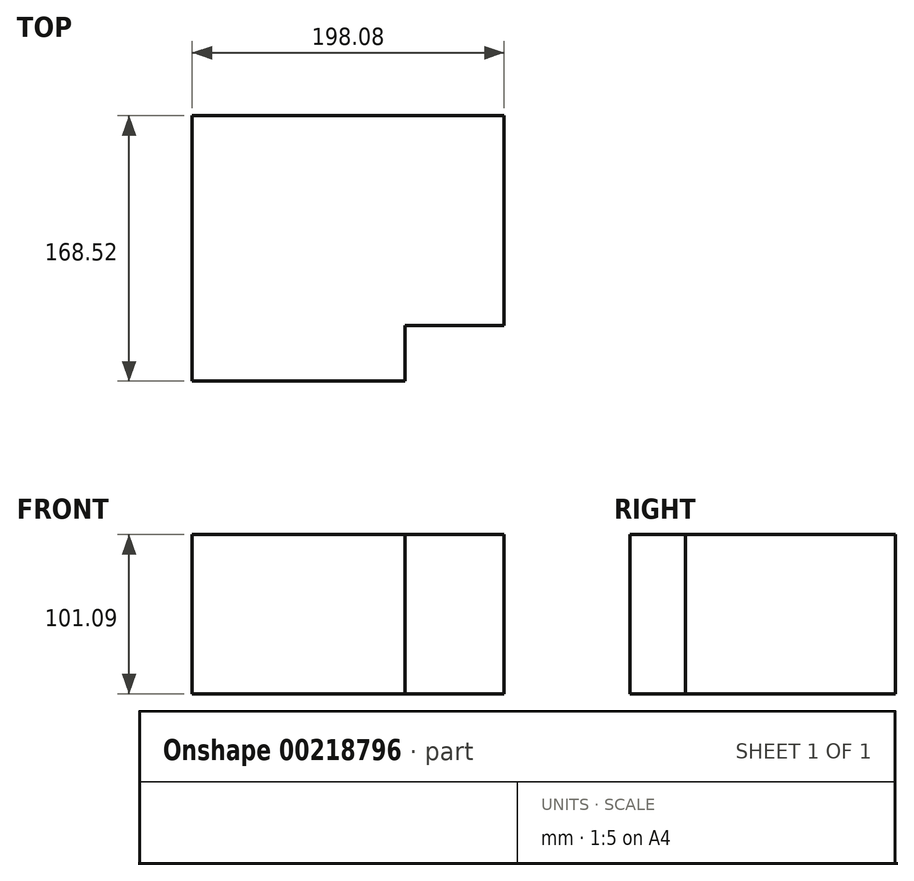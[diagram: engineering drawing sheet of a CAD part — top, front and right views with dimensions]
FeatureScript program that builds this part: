
annotation { "Feature Type Name" : "Feature", "Feature Type Description" : "" }
export const myFeature = defineFeature(function(context is Context, id is Id, definition is map)
    precondition{}
    {
        {
            var Q0;
            Q0=qCreatedBy(makeId("Top.planeOp"),FACE);
            var sketch = newSketch(context, id + "F0", { "sketchPlane" : qUnion([Q0])});
            skLineSegment(sketch, "E0.top", {"start": v(-99.04, 66.68) * mm, "end": v(99.04, 66.68) * mm});
            skLineSegment(sketch, "E0.left", {"start": v(-99.04, -66.68) * mm, "end": v(-99.04, 66.68) * mm});
            skLineSegment(sketch, "E0.right", {"start": v(99.04, -66.68) * mm, "end": v(99.04, 66.68) * mm});
            skPoint(sketch, "E0.middle", {"position": v(0, 0) * mm});
            skLineSegment(sketch, "E1.top", {"start": v(13.38, -101.84) * mm, "end": v(36.08, -101.84) * mm});
            skLineSegment(sketch, "E1.right", {"start": v(36.08, -66.68) * mm, "end": v(36.08, -101.84) * mm});
            skLineSegment(sketch, "E2.trimOffspring", {"start": v(36.08, -66.68) * mm, "end": v(99.04, -66.68) * mm});
            skLineSegment(sketch, "E3", {"start": v(13.38, -101.84) * mm, "end": v(-99.04, -101.84) * mm});
            skLineSegment(sketch, "E4", {"start": v(-99.04, -101.84) * mm, "end": v(-99.04, -66.68) * mm});
            skSolve(sketch);
        }
        {
            var Q0;
            Q0=makeQuery(id+"F0.imprint","IMPRINT",FACE,{"disambiguationData":[TD([[makeQuery(id+"F0.imprint","IMPRINT",EDGE,{"derivedFrom":sQuery(id+"F0.wireOp",EDGE,"E0.top")}),-1.0]])]});
            extrude(context, id + "F1", {"entities" : qUnion([Q0]), "depth" : 101.1 * mm});
        }
    });
